# Revit family: PRD_AR_HsptlPttrnPlstrSnks_PlasterSink_SIRX835,836
name_source: partatom
category: Plumbing Fixtures
revit_build: Autodesk Revit 2018 (Build: 20190510_1515(x64)
units: mm (PartAtom-declared; Revit-internal decimal feet)

## family parameters
Cut with Voids When Loaded = No
Host = Face
OmniClass Number = 23.45.05.14.14
OmniClass Title = Sinks/Lavatories
Part Type = Normal
Room Calculation Point = No
Round Connector Dimension = Use Diameter
Shared = No

## types (2) — shared parameters
AssetType = Fixed
Category = Pr_40_20_96_39, Hospital pattern plaster sinks
Color = stainless steel
Default Elevation = 903 mm  [stored 2.9626 ft]
DrainSize = DN 40 (1 1/2 inch.)
DurationUnit = year
Features = stainless steel, 1.20 mm, satin finished, worktop mounting, 1000x420x600 mm (WxHxD)
Finish = satin finished
FinishAndMaterial = stainless steel
Form = Plaster sink for work top mounting, stainless steel, surface satin finished
GrossWeight = 18.72 kg
IfcExportAs = IfcSanitaryTerminalType
IfcExportType = SINK
IntegralAccessories = Lugs for underneath mounting are included
Manufacturer = KWC Group AG
ManufacturerName = KWC Group AG
ManufacturerURL = www.kwc.com
Material = stainless steel
MaterialsBody = Stainless steel 1.4301
MaterialsFinishAndColour = Satin finished
NBSDescription = Hospital pattern plaster sinks
NBSReference = 45-35-70/343
NetWeight = 18.70 kg
NominalDepth = 420 mm  [stored 1.37795 ft]
NominalHeight = 420 mm  [stored 1.37795 ft]
NominalLength = 600 mm  [stored 1.9685 ft]
NominalWidth = 1000 mm  [stored 3.28084 ft]
ProductInformation = https://pim.kwc.com
Shape = Rectangular
SinkMounting = CounterTop
SinkType = Plaster
Size = 1000 x 420 x 600 mm
URL = www.kwc.com
Uniclass2015Code = Pr_40_20_96_39
Uniclass2015Title = Hospital pattern plaster sinks
Uniclass2015Version = Products v1.10
Version = 1
WarrantyDurationUnit = year
WashHandBasinMounting = CounterTop
WashHandBasinType = HandRinse
WashbasinMaterial = PRD_AR_StainlessSteel_SatinFinished
WasteSize = 40  [stored 0.131234 ft]
WaterSupplyOverflowAndWasteHolesOverflow = no
WaterSupplyOverflowAndWasteHolesWaste = Center-Center
WaterSupplyOverflowAndWasteHolesWaterSupply = no taphole

## per-type parameters (varying)
| type | BIMObjectName | Description | Hand | ModelNumber | Name | WasteOffset |
| SIRX835 | PRD_AR_HospitalPatternPlasterSinks_PlasterSink_SIRX835 | Plaster sink for work top mounting, stainless steel, surface satin finished, material thickness 1.2 mm, drain board left, seamless welded bowl with diameter 450x500x200 mm, bowl and drain board with revolving channel, 1 1/2 inch centric waste hole punch, removable plaster basket with cover. drainboard left. | drainboard left | 2000071901 | Sirius Plaster Sink SIRX835 | 680 mm |
| SIRX836 | PRD_AR_HospitalPatternPlasterSinks_PlasterSink_SIRX836 | Plaster sink for work top mounting, stainless steel, surface satin finished, material thickness 1.2 mm, drain board right, seamless welded bowl with diameter 450x500x200 mm, bowl and drain board with revolving channel, 1 1/2 inch centric waste hole punch, removable plaster basket with cover. drainboard right. | drainboard right | 2000071902 | Sirius Plaster Sink SIRX836 | 320 mm  [stored 1.04987 ft] |

note: column(s) folded — value = type name in every type: Model, ModelReference, Type

note: [stored X ft] marks values corroborated as IEEE doubles in the binary element streams (Revit-internal decimal feet)

## geometry (parser evidence)
native form markers: Sweep x30
no freeform markers — native parametric forms only
